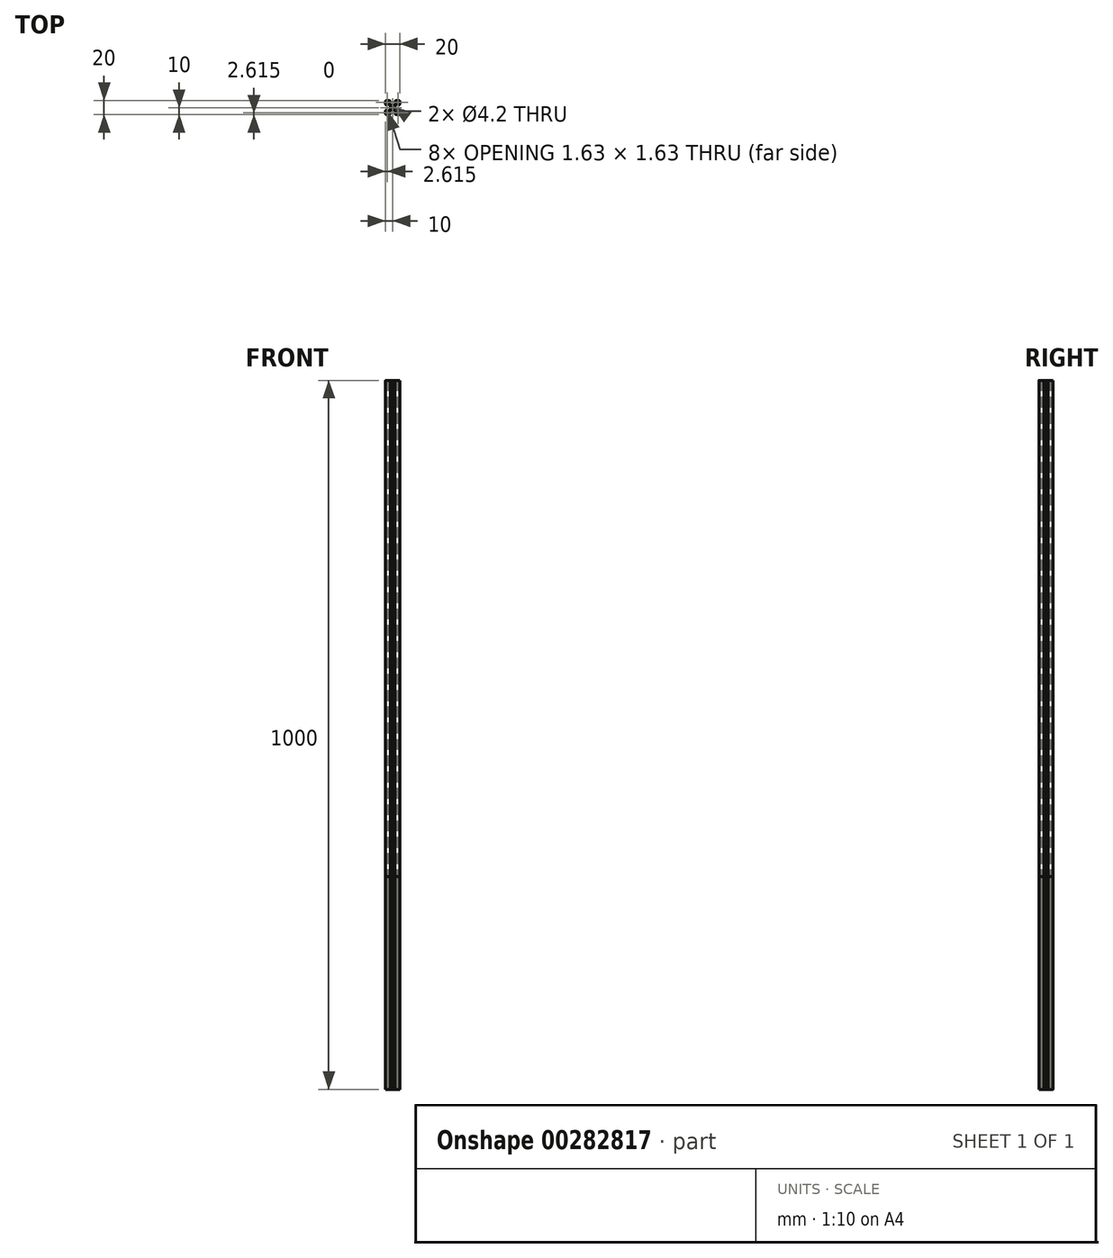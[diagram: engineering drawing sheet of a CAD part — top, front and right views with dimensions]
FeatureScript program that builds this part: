
annotation { "Feature Type Name" : "Feature", "Feature Type Description" : "" }
export const myFeature = defineFeature(function(context is Context, id is Id, definition is map)
    precondition{}
    {
        {
            var Q0;
            Q0=qCreatedBy(makeId("Top.planeOp"),FACE);
            var sketch = newSketch(context, id + "F0", { "sketchPlane" : qUnion([Q0])});
            skLineSegment(sketch, "E0", {"start": v(0, 0) * mm, "end": v(-3.5, 0) * mm, "construction": true});
            skLineSegment(sketch, "E1", {"start": v(0, 0) * mm, "end": v(0, -3.5) * mm, "construction": true});
            skLineSegment(sketch, "E2", {"start": v(0, 0) * mm, "end": v(-10, -10) * mm, "construction": true});
            skLineSegment(sketch, "E3", {"start": v(-3.5, -0.1) * mm, "end": v(-3.5, -2.44) * mm});
            skLineSegment(sketch, "E4", {"start": v(-3.5, -2.44) * mm, "end": v(-6.56, -5.5) * mm});
            skLineSegment(sketch, "E5", {"start": v(-6.56, -5.5) * mm, "end": v(-8.2, -5.5) * mm});
            skLineSegment(sketch, "E6", {"start": v(-8.2, -5.5) * mm, "end": v(-8.2, -2.9) * mm});
            skLineSegment(sketch, "E7", {"start": v(-8.2, -2.9) * mm, "end": v(-8.3, -2.9) * mm});
            skLineSegment(sketch, "E8", {"start": v(-8.3, -2.9) * mm, "end": v(-9.77, -4.35) * mm});
            skLineSegment(sketch, "E9", {"start": v(-10, -4.9) * mm, "end": v(-10, -8.5) * mm});
            skPoint(sketch, "E10.visualSharp", {"position": v(-10, -4.58) * mm});
            skArc(sketch, "E10.filletArc", {"start": v(-9.77, -4.35) * mm, "mid": v(-9.94, -4.6) * mm, "end": v(-10, -4.9) * mm});
            skLineSegment(sketch, "E11", {"start": v(-7.12, -7.12) * mm, "end": v(-7.66, -6.57) * mm});
            skLineSegment(sketch, "E12", {"start": v(-7.66, -6.57) * mm, "end": v(-8.2, -6.57) * mm});
            skLineSegment(sketch, "E13", {"start": v(-8.2, -6.57) * mm, "end": v(-8.2, -8.2) * mm});
            skLineSegment(sketch, "E14.MirrorCS", {"start": v(-4.9, -10) * mm, "end": v(-8.5, -10) * mm});
            skArc(sketch, "E15.MirrorCS", {"start": v(-4.35, -9.77) * mm, "mid": v(-4.6, -9.94) * mm, "end": v(-4.9, -10) * mm});
            skLineSegment(sketch, "E16.MirrorCS", {"start": v(-2.89, -8.3) * mm, "end": v(-4.35, -9.77) * mm});
            skLineSegment(sketch, "E17.MirrorCS", {"start": v(-5.5, -8.2) * mm, "end": v(-2.89, -8.2) * mm});
            skLineSegment(sketch, "E18.MirrorCS", {"start": v(-5.5, -6.56) * mm, "end": v(-5.5, -8.2) * mm});
            skLineSegment(sketch, "E19.MirrorCS", {"start": v(-2.44, -3.5) * mm, "end": v(-5.5, -6.56) * mm});
            skLineSegment(sketch, "E20.MirrorCS", {"start": v(-0.1, -3.5) * mm, "end": v(-2.44, -3.5) * mm});
            skLineSegment(sketch, "E21.MirrorCS", {"start": v(-6.57, -8.2) * mm, "end": v(-8.2, -8.2) * mm});
            skLineSegment(sketch, "E22.MirrorCS", {"start": v(-6.57, -7.66) * mm, "end": v(-6.57, -8.2) * mm});
            skLineSegment(sketch, "E23.MirrorCS", {"start": v(-7.11, -7.12) * mm, "end": v(-6.57, -7.66) * mm});
            skPoint(sketch, "E24.visualSharp", {"position": v(-10, -10) * mm});
            skArc(sketch, "E24.filletArc", {"start": v(-10, -8.5) * mm, "mid": v(-9.56, -9.56) * mm, "end": v(-8.5, -10) * mm});
            skLineSegment(sketch, "E25.MirrorCS", {"start": v(-2.89, -8.2) * mm, "end": v(-2.89, -8.3) * mm});
            skLineSegment(sketch, "E26.MirrorCS", {"start": v(0.1, -3.5) * mm, "end": v(2.44, -3.5) * mm});
            skLineSegment(sketch, "E27.MirrorCS", {"start": v(2.44, -3.5) * mm, "end": v(5.5, -6.56) * mm});
            skLineSegment(sketch, "E28.MirrorCS", {"start": v(5.5, -6.56) * mm, "end": v(5.5, -8.2) * mm});
            skLineSegment(sketch, "E29.MirrorCS", {"start": v(2.89, -8.2) * mm, "end": v(2.89, -8.3) * mm});
            skLineSegment(sketch, "E30.MirrorCS", {"start": v(2.89, -8.3) * mm, "end": v(4.35, -9.77) * mm});
            skLineSegment(sketch, "E31.MirrorCS", {"start": v(5.5, -8.2) * mm, "end": v(2.89, -8.2) * mm});
            skArc(sketch, "E32.MirrorCS", {"start": v(4.35, -9.77) * mm, "mid": v(4.6, -9.94) * mm, "end": v(4.9, -10) * mm});
            skLineSegment(sketch, "E33.MirrorCS", {"start": v(4.9, -10) * mm, "end": v(8.5, -10) * mm});
            skArc(sketch, "E34.MirrorCS", {"start": v(10, -8.5) * mm, "mid": v(9.56, -9.56) * mm, "end": v(8.5, -10) * mm});
            skLineSegment(sketch, "E35.MirrorCS", {"start": v(10, -4.9) * mm, "end": v(10, -8.5) * mm});
            skArc(sketch, "E36.MirrorCS", {"start": v(9.77, -4.35) * mm, "mid": v(9.94, -4.6) * mm, "end": v(10, -4.9) * mm});
            skLineSegment(sketch, "E37.MirrorCS", {"start": v(8.2, -5.5) * mm, "end": v(8.2, -2.9) * mm});
            skLineSegment(sketch, "E38.MirrorCS", {"start": v(8.2, -2.9) * mm, "end": v(8.3, -2.9) * mm});
            skLineSegment(sketch, "E39.MirrorCS", {"start": v(8.3, -2.9) * mm, "end": v(9.77, -4.35) * mm});
            skLineSegment(sketch, "E40.MirrorCS", {"start": v(6.56, -5.5) * mm, "end": v(8.2, -5.5) * mm});
            skLineSegment(sketch, "E41.MirrorCS", {"start": v(3.5, -2.44) * mm, "end": v(6.56, -5.5) * mm});
            skLineSegment(sketch, "E42.MirrorCS", {"start": v(3.5, -0.1) * mm, "end": v(3.5, -2.44) * mm});
            skLineSegment(sketch, "E43.MirrorCS", {"start": v(7.12, -7.12) * mm, "end": v(7.66, -6.57) * mm});
            skLineSegment(sketch, "E44.MirrorCS", {"start": v(7.66, -6.57) * mm, "end": v(8.2, -6.57) * mm});
            skLineSegment(sketch, "E45.MirrorCS", {"start": v(8.2, -6.57) * mm, "end": v(8.2, -8.2) * mm});
            skLineSegment(sketch, "E46.MirrorCS", {"start": v(6.57, -8.2) * mm, "end": v(8.2, -8.2) * mm});
            skLineSegment(sketch, "E47.MirrorCS", {"start": v(6.57, -7.66) * mm, "end": v(6.57, -8.2) * mm});
            skLineSegment(sketch, "E48.MirrorCS", {"start": v(7.11, -7.12) * mm, "end": v(6.57, -7.66) * mm});
            skLineSegment(sketch, "E49.MirrorCS", {"start": v(7.66, 6.57) * mm, "end": v(8.2, 6.57) * mm});
            skLineSegment(sketch, "E50.MirrorCS", {"start": v(7.12, 7.12) * mm, "end": v(7.66, 6.57) * mm});
            skLineSegment(sketch, "E51.MirrorCS", {"start": v(0.1, 3.5) * mm, "end": v(2.44, 3.5) * mm});
            skLineSegment(sketch, "E52.MirrorCS", {"start": v(6.57, 7.66) * mm, "end": v(6.57, 8.2) * mm});
            skLineSegment(sketch, "E53.MirrorCS", {"start": v(8.2, 2.9) * mm, "end": v(8.3, 2.9) * mm});
            skArc(sketch, "E54.MirrorCS", {"start": v(9.77, 4.35) * mm, "mid": v(9.94, 4.6) * mm, "end": v(10, 4.9) * mm});
            skLineSegment(sketch, "E55.MirrorCS", {"start": v(7.11, 7.12) * mm, "end": v(6.57, 7.66) * mm});
            skLineSegment(sketch, "E56.MirrorCS", {"start": v(2.89, 8.2) * mm, "end": v(2.89, 8.3) * mm});
            skArc(sketch, "E57.MirrorCS", {"start": v(4.35, 9.77) * mm, "mid": v(4.6, 9.94) * mm, "end": v(4.9, 10) * mm});
            skLineSegment(sketch, "E58.MirrorCS", {"start": v(6.56, 5.5) * mm, "end": v(8.2, 5.5) * mm});
            skLineSegment(sketch, "E59.MirrorCS", {"start": v(5.5, 6.56) * mm, "end": v(5.5, 8.2) * mm});
            skLineSegment(sketch, "E60.MirrorCS", {"start": v(6.57, 8.2) * mm, "end": v(8.2, 8.2) * mm});
            skLineSegment(sketch, "E61.MirrorCS", {"start": v(10, 4.9) * mm, "end": v(10, 8.5) * mm});
            skLineSegment(sketch, "E62.MirrorCS", {"start": v(8.3, 2.9) * mm, "end": v(9.77, 4.35) * mm});
            skLineSegment(sketch, "E63.MirrorCS", {"start": v(4.9, 10) * mm, "end": v(8.5, 10) * mm});
            skLineSegment(sketch, "E64.MirrorCS", {"start": v(2.44, 3.5) * mm, "end": v(5.5, 6.56) * mm});
            skLineSegment(sketch, "E65.MirrorCS", {"start": v(3.5, 2.44) * mm, "end": v(6.56, 5.5) * mm});
            skLineSegment(sketch, "E66.MirrorCS", {"start": v(5.5, 8.2) * mm, "end": v(2.89, 8.2) * mm});
            skLineSegment(sketch, "E67.MirrorCS", {"start": v(8.2, 5.5) * mm, "end": v(8.2, 2.9) * mm});
            skLineSegment(sketch, "E68.MirrorCS", {"start": v(2.89, 8.3) * mm, "end": v(4.35, 9.77) * mm});
            skLineSegment(sketch, "E69.MirrorCS", {"start": v(3.5, 0.1) * mm, "end": v(3.5, 2.44) * mm});
            skLineSegment(sketch, "E70.MirrorCS", {"start": v(8.2, 6.57) * mm, "end": v(8.2, 8.2) * mm});
            skArc(sketch, "E71.MirrorCS", {"start": v(10, 8.5) * mm, "mid": v(9.56, 9.56) * mm, "end": v(8.5, 10) * mm});
            skLineSegment(sketch, "E72.MirrorCS", {"start": v(-2.89, 8.2) * mm, "end": v(-2.89, 8.3) * mm});
            skLineSegment(sketch, "E73.MirrorCS", {"start": v(-5.5, 6.56) * mm, "end": v(-5.5, 8.2) * mm});
            skArc(sketch, "E74.MirrorCS", {"start": v(-4.35, 9.77) * mm, "mid": v(-4.6, 9.94) * mm, "end": v(-4.9, 10) * mm});
            skLineSegment(sketch, "E75.MirrorCS", {"start": v(-4.9, 10) * mm, "end": v(-8.5, 10) * mm});
            skLineSegment(sketch, "E76.MirrorCS", {"start": v(-2.89, 8.3) * mm, "end": v(-4.35, 9.77) * mm});
            skLineSegment(sketch, "E77.MirrorCS", {"start": v(-5.5, 8.2) * mm, "end": v(-2.89, 8.2) * mm});
            skLineSegment(sketch, "E78.MirrorCS", {"start": v(-2.44, 3.5) * mm, "end": v(-5.5, 6.56) * mm});
            skLineSegment(sketch, "E79.MirrorCS", {"start": v(-0.1, 3.5) * mm, "end": v(-2.44, 3.5) * mm});
            skLineSegment(sketch, "E80.MirrorCS", {"start": v(-3.5, 0.1) * mm, "end": v(-3.5, 2.44) * mm});
            skLineSegment(sketch, "E81.MirrorCS", {"start": v(-3.5, 2.44) * mm, "end": v(-6.56, 5.5) * mm});
            skLineSegment(sketch, "E82.MirrorCS", {"start": v(-6.56, 5.5) * mm, "end": v(-8.2, 5.5) * mm});
            skLineSegment(sketch, "E83.MirrorCS", {"start": v(-8.2, 2.9) * mm, "end": v(-8.3, 2.9) * mm});
            skLineSegment(sketch, "E84.MirrorCS", {"start": v(-8.2, 5.5) * mm, "end": v(-8.2, 2.9) * mm});
            skLineSegment(sketch, "E85.MirrorCS", {"start": v(-8.3, 2.9) * mm, "end": v(-9.77, 4.35) * mm});
            skLineSegment(sketch, "E86.MirrorCS", {"start": v(-6.57, 7.66) * mm, "end": v(-6.57, 8.2) * mm});
            skLineSegment(sketch, "E87.MirrorCS", {"start": v(-6.57, 8.2) * mm, "end": v(-8.2, 8.2) * mm});
            skLineSegment(sketch, "E88.MirrorCS", {"start": v(-7.11, 7.12) * mm, "end": v(-6.57, 7.66) * mm});
            skLineSegment(sketch, "E89.MirrorCS", {"start": v(-7.12, 7.12) * mm, "end": v(-7.66, 6.57) * mm});
            skLineSegment(sketch, "E90.MirrorCS", {"start": v(-7.66, 6.57) * mm, "end": v(-8.2, 6.57) * mm});
            skLineSegment(sketch, "E91.MirrorCS", {"start": v(-8.2, 6.57) * mm, "end": v(-8.2, 8.2) * mm});
            skArc(sketch, "E92.MirrorCS", {"start": v(-9.77, 4.35) * mm, "mid": v(-9.94, 4.6) * mm, "end": v(-10, 4.9) * mm});
            skArc(sketch, "E93.MirrorCS", {"start": v(-10, 8.5) * mm, "mid": v(-9.56, 9.56) * mm, "end": v(-8.5, 10) * mm});
            skLineSegment(sketch, "E94.MirrorCS", {"start": v(-10, 4.9) * mm, "end": v(-10, 8.5) * mm});
            skCircle(sketch, "E95", {"center": v(0, 0) * mm, "radius": 2.1 * mm});
            skLineSegment(sketch, "E96", {"start": v(-3.5, -0.1) * mm, "end": v(-3.4, 0) * mm});
            skLineSegment(sketch, "E97.MirrorCS", {"start": v(-3.5, 0.1) * mm, "end": v(-3.4, 0) * mm});
            skPoint(sketch, "E98.orphan", {"position": v(-3.5, 0) * mm});
            skLineSegment(sketch, "E99.MirrorCS", {"start": v(-0.1, -3.5) * mm, "end": v(0, -3.4) * mm});
            skLineSegment(sketch, "E100.MirrorCS", {"start": v(0.1, -3.5) * mm, "end": v(0, -3.4) * mm});
            skLineSegment(sketch, "E101.MirrorCS", {"start": v(0.1, 3.5) * mm, "end": v(0, 3.4) * mm});
            skLineSegment(sketch, "E102.MirrorCS", {"start": v(-0.1, 3.5) * mm, "end": v(0, 3.4) * mm});
            skLineSegment(sketch, "E103.MirrorCS", {"start": v(3.5, 0.1) * mm, "end": v(3.4, 0) * mm});
            skLineSegment(sketch, "E104.MirrorCS", {"start": v(3.5, -0.1) * mm, "end": v(3.4, 0) * mm});
            skPoint(sketch, "E105.orphan", {"position": v(0, -3.5) * mm});
            skPoint(sketch, "E106.orphan", {"position": v(3.5, 0) * mm});
            skPoint(sketch, "E107.orphan", {"position": v(0, 3.5) * mm});
            skSolve(sketch);
        }
        {
            var Q0;
            Q0=qSketchRegion(id+"F0",true);
            extrude(context, id + "F1", {"entities" : qUnion([Q0]), "depth" : 1000 * mm});
        }
        {
            var Q0;
            Q0=qSketchRegion(id+"F0",true);
            extrude(context, id + "F2", {"entities" : qUnion([Q0]), "depth" : 300 * mm});
        }
    });
